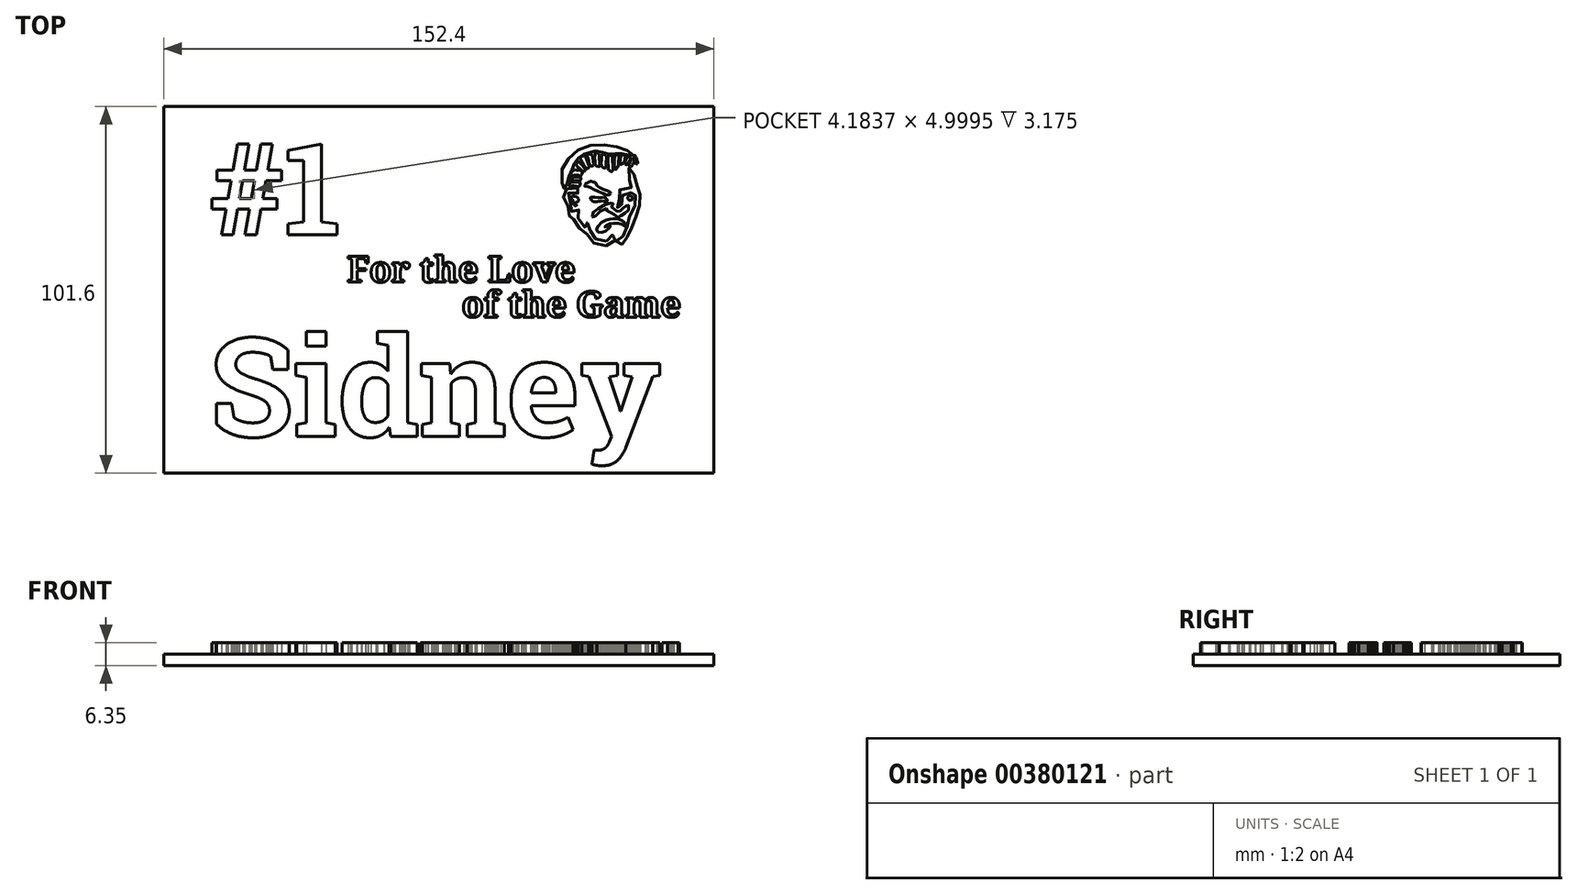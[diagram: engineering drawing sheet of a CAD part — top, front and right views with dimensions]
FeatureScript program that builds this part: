
annotation { "Feature Type Name" : "Feature", "Feature Type Description" : "" }
export const myFeature = defineFeature(function(context is Context, id is Id, definition is map)
    precondition{}
    {
        {
            var Q0;
            Q0=qCreatedBy(makeId("Top.planeOp"),FACE);
            var sketch = newSketch(context, id + "F0", { "sketchPlane" : qUnion([Q0])});
            skLineSegment(sketch, "E0.bottom", {"start": v(-75.13, 26) * mm, "end": v(77.27, 26) * mm});
            skLineSegment(sketch, "E0.top", {"start": v(-75.13, -75.6) * mm, "end": v(77.27, -75.6) * mm});
            skLineSegment(sketch, "E0.left", {"start": v(-75.13, 26) * mm, "end": v(-75.13, -75.6) * mm});
            skLineSegment(sketch, "E0.right", {"start": v(77.27, 26) * mm, "end": v(77.27, -75.6) * mm});
            skSolve(sketch);
        }
        {
            var Q0;
            Q0=makeQuery(id+"F0.imprint","IMPRINT",FACE,{"disambiguationData":[TD([[makeQuery(id+"F0.imprint","IMPRINT",EDGE,{"derivedFrom":sQuery(id+"F0.wireOp",EDGE,"E0.bottom")}),-1.0]])]});
            var sketch = newSketch(context, id + "F1", { "sketchPlane" : qUnion([Q0])});
            skFitSpline(sketch, "E1", {"points": [v(47.57, -11.3) * mm, v(48.35, -11.04) * mm, v(48.7, -10.35) * mm, v(49.04, -9.7) * mm, v(49.57, -9.46) * mm, v(50.02, -9.78) * mm, v(50.06, -10.58) * mm, v(49.74, -11.5) * mm, v(49.1, -12.15) * mm, v(47.63, -12.55) * mm, v(46.12, -12.5) * mm, v(44.61, -12.12) * mm, v(43.38, -11.34) * mm, v(42.6, -10.32) * mm, v(42.24, -9.52) * mm, v(42.15, -9.31) * mm, v(41.34, -8.82) * mm, v(40.33, -8.02) * mm, v(39.44, -7.2) * mm, v(38.67, -6.1) * mm, v(38.42, -5) * mm, v(38.42, -4.22) * mm, v(38.35, -4.2) * mm, v(37.68, -4.39) * mm, v(37.16, -4.27) * mm, v(36.95, -3.72) * mm, v(36.86, -2.5) * mm, v(36.8, -1.48) * mm, v(36.67, -1.07) * mm, v(35.77, 0.2) * mm, v(35.58, 1.07) * mm, v(35.86, 2.13) * mm, v(36.18, 2.7) * mm, v(36.53, 3.12) * mm, v(37.23, 3.22) * mm, v(39.03, 3.4) * mm, v(39.82, 3.34) * mm, v(40.19, 3.09) * mm, v(40.23, 2.45) * mm, v(39.66, 1.98) * mm, v(38.93, 1.9) * mm, v(38.59, 2.03) * mm, v(37.24, 2.03) * mm, v(36.72, 1.65) * mm, v(36.72, 0.85) * mm, v(37.32, -0.2) * mm, v(37.77, -1.18) * mm, v(37.85, -2.09) * mm, v(37.9, -3.1) * mm, v(37.99, -3.1) * mm, v(38.63, -3.1) * mm, v(39.4, -2.76) * mm, v(39.72, -2.59) * mm, v(39.8, -2.7) * mm, v(39.73, -3.22) * mm, v(39.6, -4) * mm, v(39.6, -4.77) * mm, v(40.1, -5.82) * mm, v(41.16, -7.15) * mm, v(41.6, -7.53) * mm, v(41.9, -7.56) * mm, v(41.89, -7.44) * mm, v(41.82, -6.61) * mm, v(42, -6.23) * mm, v(42.5, -6.3) * mm, v(42.8, -6.61) * mm, v(43.05, -7.98) * mm, v(43.22, -8.82) * mm, v(43.51, -9.54) * mm, v(44.12, -10.4) * mm, v(45.11, -11.01) * mm, v(46.32, -11.33) * mm, v(47.57, -11.3) * mm]});
            skFitSpline(sketch, "E2", {"points": [v(47.8, -7.3) * mm, v(47.13, -7.42) * mm, v(47.01, -7.42) * mm, v(47.13, -7.18) * mm, v(48.11, -6.65) * mm, v(49.11, -6.46) * mm, v(50.54, -6.45) * mm, v(51.76, -6.67) * mm, v(52.61, -7.21) * mm, v(52.82, -7.33) * mm, v(52.97, -7.12) * mm, v(52.7, -6.5) * mm, v(52.11, -5.74) * mm, v(50.6, -5.18) * mm, v(49.08, -5.16) * mm, v(48.46, -5.24) * mm, v(47.16, -5.6) * mm, v(45.65, -6.61) * mm, v(44.86, -7.78) * mm, v(44.9, -8.5) * mm, v(45.47, -8.94) * mm, v(46.7, -8.8) * mm, v(47.75, -8.16) * mm, v(48.56, -7.4) * mm, v(48.6, -7.12) * mm, v(47.8, -7.3) * mm]});
            skFitSpline(sketch, "E3", {"points": [v(51.85, -12.22) * mm, v(51.05, -12.44) * mm, v(50.33, -12.28) * mm, v(50.13, -11.73) * mm, v(50.52, -11.04) * mm, v(51.15, -10.86) * mm, v(51.76, -10.57) * mm, v(52.13, -10) * mm, v(52.3, -9.2) * mm, v(52.67, -8.25) * mm, v(53.2, -7.5) * mm, v(53.55, -6.76) * mm, v(53.63, -5.82) * mm, v(53.78, -4.85) * mm, v(54.49, -3.73) * mm, v(55.3, -2.73) * mm, v(55.42, -1.6) * mm, v(55.17, -0.4) * mm, v(55.2, 0.11) * mm, v(55.52, 1.32) * mm, v(55.57, 2.16) * mm, v(55.47, 2.42) * mm, v(54.99, 2.38) * mm, v(54.56, 2.14) * mm, v(53.7, 2.1) * mm, v(52.55, 2.06) * mm, v(52.07, 1.77) * mm, v(51.98, 1.02) * mm, v(52.2, 0.28) * mm, v(52.08, -0.6) * mm, v(51.72, -1.24) * mm, v(51.47, -1.75) * mm, v(51.5, -2.22) * mm, v(51.32, -2.4) * mm, v(50.6, -2.13) * mm, v(50.38, -1.6) * mm, v(50.64, -0.97) * mm, v(51, -0.17) * mm, v(51.06, 0.44) * mm, v(50.78, 1.07) * mm, v(50.66, 1.97) * mm, v(51.18, 2.9) * mm, v(52.12, 3.24) * mm, v(53.3, 3.36) * mm, v(54.52, 3.48) * mm, v(54.66, 3.6) * mm, v(54.38, 3.97) * mm, v(54, 4.8) * mm, v(53.79, 6.28) * mm, v(53.9, 7.94) * mm, v(53.79, 8.9) * mm, v(53.79, 9.1) * mm, v(54.03, 9.04) * mm, v(54.76, 8.52) * mm, v(55.13, 7.38) * mm, v(55.34, 5.97) * mm, v(55.56, 4.72) * mm, v(56.14, 3.87) * mm, v(56.71, 3.56) * mm, v(57.08, 2.91) * mm, v(56.95, 1.93) * mm, v(56.51, 0.55) * mm, v(56.4, -0.31) * mm, v(56.62, -1.36) * mm, v(56.69, -2.19) * mm, v(56.32, -3.56) * mm, v(55.4, -4.86) * mm, v(54.62, -5.8) * mm, v(54.5, -7.08) * mm, v(54.37, -8.24) * mm, v(53.76, -9.26) * mm, v(53.43, -9.82) * mm, v(53.28, -10.59) * mm, v(53.14, -11.27) * mm, v(52.34, -11.95) * mm, v(51.85, -12.22) * mm]});
            skFitSpline(sketch, "E4", {"points": [v(51.65, -4.28) * mm, v(52.13, -3.81) * mm, v(53.02, -3.37) * mm, v(53.66, -2.72) * mm, v(53.77, -1.9) * mm, v(53.38, -1.13) * mm, v(53.21, -1.15) * mm, v(53, -1.68) * mm, v(52.43, -2.14) * mm, v(51.8, -2.46) * mm, v(51.42, -2.92) * mm, v(50.93, -3.27) * mm, v(50.6, -3.17) * mm, v(50.13, -2.68) * mm, v(49.7, -2.46) * mm, v(49.28, -2.45) * mm, v(49, -1.98) * mm, v(49.06, -1.41) * mm, v(49.39, -0.94) * mm, v(49.4, -0.71) * mm, v(48.82, -0.74) * mm, v(47.56, -0.99) * mm, v(45.6, -2.02) * mm, v(44.06, -3.24) * mm, v(43.57, -3.77) * mm, v(43.7, -4.86) * mm, v(43.9, -4.88) * mm, v(44.45, -4.27) * mm, v(46.1, -2.93) * mm, v(47.41, -2.3) * mm, v(47.63, -2.3) * mm, v(47.73, -2.85) * mm, v(48.15, -3.33) * mm, v(48.9, -3.44) * mm, v(49.24, -3.55) * mm, v(49.84, -4.18) * mm, v(50.54, -4.68) * mm, v(51.18, -4.66) * mm, v(51.65, -4.28) * mm]});
            skFitSpline(sketch, "E5", {"points": [v(54.73, 0.39) * mm, v(54.77, 0.82) * mm, v(54.18, 1.2) * mm, v(53.55, 1.02) * mm, v(53.47, 0.3) * mm, v(54.02, 0) * mm, v(54.73, 0.39) * mm]});
            skFitSpline(sketch, "E6", {"points": [v(44.44, -0.47) * mm, v(43.66, -0.25) * mm, v(43.08, 0.44) * mm, v(43.14, 0.75) * mm, v(43.78, 0.8) * mm, v(46.74, 0.78) * mm, v(47.17, 0.7) * mm, v(47.78, -0.13) * mm, v(47.64, -0.32) * mm, v(46.64, -0.26) * mm, v(45.29, -0.32) * mm, v(44.44, -0.47) * mm]});
            skFitSpline(sketch, "E7", {"points": [v(46.65, 1.86) * mm, v(47.46, 1.48) * mm, v(48.33, 1.53) * mm, v(48.69, 2.02) * mm, v(48.54, 2.32) * mm, v(47.26, 2.83) * mm, v(45.32, 3.72) * mm, v(44.79, 4.23) * mm, v(44.53, 4.83) * mm, v(44.13, 5) * mm, v(43.88, 5) * mm, v(43.34, 5.26) * mm, v(43.09, 5.3) * mm, v(42.9, 5.05) * mm, v(42.6, 5.07) * mm, v(42.3, 4.85) * mm, v(42.2, 4.73) * mm, v(41.9, 4.72) * mm, v(41.8, 4.5) * mm, v(41.38, 4.05) * mm, v(41.56, 3.84) * mm, v(42.59, 3.74) * mm, v(43.78, 3.19) * mm, v(46.65, 1.86) * mm]});
            skFitSpline(sketch, "E8", {"points": [v(39.09, -1.2) * mm, v(38.85, -1.02) * mm, v(39.04, -0.63) * mm, v(39.6, -0.4) * mm, v(39.72, 0.33) * mm, v(39.01, 1.06) * mm, v(38.23, 1.1) * mm, v(37.7, 0.65) * mm, v(37.83, 0.29) * mm, v(38.12, 0.15) * mm, v(38.31, -0.34) * mm, v(38.52, -1.23) * mm, v(38.92, -1.63) * mm, v(39.18, -1.51) * mm, v(39.26, -1.2) * mm, v(39.09, -1.2) * mm]});
            skFitSpline(sketch, "E9", {"points": [v(35.18, 4.73) * mm, v(35.4, 3.4) * mm, v(35.76, 3.05) * mm, v(35.87, 3.13) * mm, v(36.08, 3.42) * mm, v(36.43, 3.67) * mm, v(36.66, 4.42) * mm, v(36.6, 5.36) * mm, v(37.02, 6.1) * mm, v(37.15, 6.7) * mm, v(37.23, 7.46) * mm, v(37.88, 8.4) * mm, v(38.45, 9.02) * mm, v(38.56, 9.75) * mm, v(38.74, 10.4) * mm, v(39.17, 10.98) * mm, v(39.64, 11.29) * mm, v(39.78, 11.9) * mm, v(40.12, 12.28) * mm, v(40.85, 12.68) * mm, v(41.65, 12.77) * mm, v(42.03, 12.99) * mm, v(42.91, 13.25) * mm, v(43.49, 13.17) * mm, v(43.91, 13.25) * mm, v(44.22, 13.54) * mm, v(44.87, 13.6) * mm, v(45.62, 13.32) * mm, v(46.3, 13.31) * mm, v(46.91, 13.3) * mm, v(47.51, 12.81) * mm, v(48.11, 12.71) * mm, v(48.8, 12.83) * mm, v(49.39, 12.68) * mm, v(50.13, 12.89) * mm, v(50.83, 12.96) * mm, v(51.35, 12.83) * mm, v(51.87, 12.94) * mm, v(52.53, 12.95) * mm, v(53.18, 12.6) * mm, v(53.93, 12.6) * mm, v(54.48, 12.4) * mm, v(54.65, 12.18) * mm, v(55.03, 12.55) * mm, v(54.73, 12.89) * mm, v(53.9, 13.45) * mm, v(51.53, 14.51) * mm, v(50.44, 14.76) * mm, v(49.1, 15.08) * mm, v(45.83, 15.4) * mm, v(43.17, 15.22) * mm, v(40.97, 14.54) * mm, v(38.6, 13.18) * mm, v(36.98, 11.4) * mm, v(35.34, 9.1) * mm, v(35.2, 8.1) * mm, v(35.18, 4.73) * mm]});
            skFitSpline(sketch, "E10", {"points": [v(39.4, 5) * mm, v(39.96, 4.99) * mm, v(40.23, 4.82) * mm, v(40.1, 4) * mm, v(39.64, 3.78) * mm, v(38.94, 3.9) * mm, v(37.89, 3.94) * mm, v(37.45, 3.8) * mm, v(37.1, 4.04) * mm, v(37.54, 4.84) * mm, v(38.3, 5) * mm, v(39.4, 5) * mm]});
            skFitSpline(sketch, "E11", {"points": [v(37.48, 5.07) * mm, v(37.11, 4.96) * mm, v(36.94, 5.2) * mm, v(37.34, 5.9) * mm, v(37.75, 6.14) * mm, v(39.96, 6.47) * mm, v(40.35, 6.2) * mm, v(40.47, 5.65) * mm, v(40.11, 5.36) * mm, v(39.64, 5.4) * mm, v(38.37, 5.41) * mm, v(37.48, 5.07) * mm]});
            skFitSpline(sketch, "E12", {"points": [v(38.14, 6.82) * mm, v(39.68, 6.88) * mm, v(40, 6.74) * mm, v(40.54, 7) * mm, v(40.85, 7.85) * mm, v(40.67, 8.1) * mm, v(39.1, 8.4) * mm, v(38.41, 8.3) * mm, v(37.9, 7.73) * mm, v(37.48, 6.86) * mm, v(37.68, 6.74) * mm, v(38.14, 6.82) * mm]});
            skFitSpline(sketch, "E13", {"points": [v(39.26, 9.59) * mm, v(41, 8.1) * mm, v(41.32, 7.94) * mm, v(41.68, 8.33) * mm, v(41.53, 8.74) * mm, v(40.44, 10.1) * mm, v(39.87, 10.6) * mm, v(39.5, 10.56) * mm, v(39.13, 10.09) * mm, v(39.26, 9.59) * mm]});
            skFitSpline(sketch, "E14", {"points": [v(40.75, 10.65) * mm, v(40.33, 11.47) * mm, v(40.46, 11.98) * mm, v(41.21, 12.34) * mm, v(41.77, 12.07) * mm, v(42.13, 11.12) * mm, v(42.72, 9.33) * mm, v(42.65, 8.96) * mm, v(42.12, 8.81) * mm, v(41.62, 9.07) * mm, v(40.75, 10.65) * mm]});
            skFitSpline(sketch, "E15", {"points": [v(42.43, 11.4) * mm, v(42.21, 12.24) * mm, v(42.3, 12.64) * mm, v(43, 12.81) * mm, v(43.54, 12.53) * mm, v(43.83, 11.13) * mm, v(44, 9.88) * mm, v(43.65, 9.47) * mm, v(42.94, 9.8) * mm, v(42.43, 11.4) * mm]});
            skFitSpline(sketch, "E16", {"points": [v(44.29, 12.06) * mm, v(44.36, 12.96) * mm, v(44.5, 13.26) * mm, v(44.93, 13.17) * mm, v(45.54, 12.55) * mm, v(45.55, 11.97) * mm, v(45.6, 9.45) * mm, v(45.5, 9.32) * mm, v(44.61, 9.6) * mm, v(44.4, 10.08) * mm, v(44.29, 12.06) * mm]});
            skFitSpline(sketch, "E17", {"points": [v(46.05, 10.51) * mm, v(46.15, 9.53) * mm, v(46.62, 9.04) * mm, v(47.1, 8.88) * mm, v(47.3, 9.08) * mm, v(47.48, 10.9) * mm, v(47.53, 12.07) * mm, v(47.34, 12.46) * mm, v(46.68, 12.84) * mm, v(46.32, 12.79) * mm, v(46.17, 11.97) * mm, v(46.05, 10.51) * mm]});
            skFitSpline(sketch, "E18", {"points": [v(48.03, 8.99) * mm, v(48.11, 8.48) * mm, v(48.48, 8.11) * mm, v(48.94, 7.92) * mm, v(49.21, 8.2) * mm, v(49.24, 10.23) * mm, v(49.16, 12.1) * mm, v(48.83, 12.47) * mm, v(48.44, 12.47) * mm, v(47.98, 12) * mm, v(47.93, 10.87) * mm, v(48.03, 8.99) * mm]});
            skFitSpline(sketch, "E19", {"points": [v(49.71, 9.45) * mm, v(49.86, 8.66) * mm, v(50.13, 8.48) * mm, v(50.3, 8.75) * mm, v(50.76, 9.43) * mm, v(50.85, 10.13) * mm, v(50.93, 12.16) * mm, v(50.81, 12.6) * mm, v(50.31, 12.66) * mm, v(49.83, 12.22) * mm, v(49.7, 11.19) * mm, v(49.71, 9.45) * mm]});
            skFitSpline(sketch, "E20", {"points": [v(51.32, 10.54) * mm, v(51.4, 11.84) * mm, v(51.7, 12.52) * mm, v(52.3, 12.55) * mm, v(52.72, 12.21) * mm, v(52.63, 11.54) * mm, v(52.29, 10.26) * mm, v(51.93, 10.06) * mm, v(51.44, 9.99) * mm, v(51.32, 10.54) * mm]});
            skFitSpline(sketch, "E21", {"points": [v(52.63, 10.38) * mm, v(52.83, 11.01) * mm, v(53.35, 11.9) * mm, v(53.66, 12.08) * mm, v(54.13, 11.71) * mm, v(53.9, 10.95) * mm, v(53.35, 10.1) * mm, v(53.17, 9.86) * mm, v(52.8, 9.99) * mm, v(52.63, 10.38) * mm]});
            skFitSpline(sketch, "E22", {"points": [v(53.86, 10.18) * mm, v(53.7, 9.9) * mm, v(53.81, 9.57) * mm, v(54.15, 9.28) * mm, v(54.42, 9.39) * mm, v(55.14, 10.6) * mm, v(55.26, 11.14) * mm, v(55.02, 11.54) * mm, v(54.8, 11.61) * mm, v(54.48, 11.27) * mm, v(53.86, 10.18) * mm]});
            skFitSpline(sketch, "E23", {"points": [v(55.24, 11.7) * mm, v(55.54, 11.38) * mm, v(55.58, 10.83) * mm, v(55.47, 10.49) * mm, v(55.7, 10.04) * mm, v(55.92, 10.02) * mm, v(56.2, 10.63) * mm, v(56.05, 10.85) * mm, v(55.85, 11.61) * mm, v(55.63, 12) * mm, v(55.42, 12.46) * mm, v(55.15, 12.4) * mm, v(55.09, 11.93) * mm, v(55.24, 11.7) * mm]});
            skText(sketch, "E24", { "text": "For the Love", "fontName": "NotoSerif-Bold.ttf"});
            skText(sketch, "E25", { "text": "of the Game", "fontName": "NotoSerif-Bold.ttf"});
            skText(sketch, "E26", { "text": "Sidney", "fontName": "RobotoSlab-Bold.ttf"});
            skText(sketch, "E27", { "text": "#1", "fontName": "RobotoSlab-Bold.ttf"});
            const initialGuessF1  = {"E24": [-0.02433, -0.0227, 1, 0, 0.00716], "E25": [0.00742, -0.0324, 1, 0, 0.00716], "E26": [-0.06243, -0.06544, 1, 0, 0.02748], "E27": [-0.06243, -0.00956, 1, 0, 0.0254]};
            skSetInitialGuess(sketch, initialGuessF1);
            skSolve(sketch);
        }
        {
            var Q0;
            Q0=qSketchRegion(id+"F0",true);
            extrude(context, id + "F2", {"entities" : qUnion([Q0]), "depth" : 3.17 * mm});
        }
        {
            var Q0;
            Q0=qSketchRegion(id+"F1",true);
            extrude(context, id + "F3", {"entities" : qUnion([Q0]), "operationType" : NewBodyOperationType.ADD, "depth" : 6.35 * mm});
        }
    });
